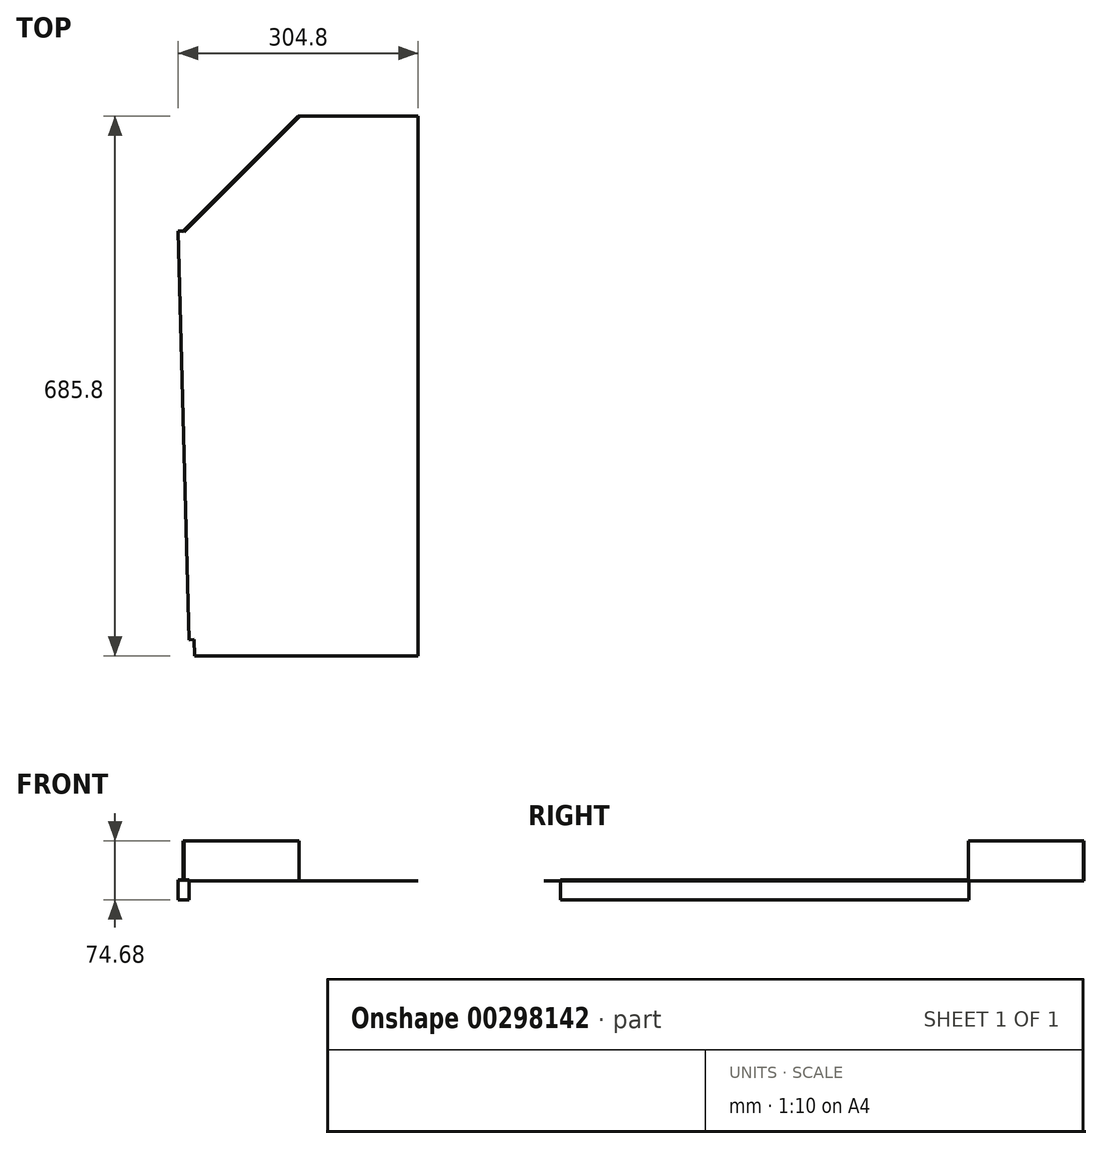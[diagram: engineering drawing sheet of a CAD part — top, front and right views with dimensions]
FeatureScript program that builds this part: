
annotation { "Feature Type Name" : "Feature", "Feature Type Description" : "" }
export const myFeature = defineFeature(function(context is Context, id is Id, definition is map)
    precondition{}
    {
        {
            assignVariable(context, id + "F0", {"name" : "thk", "anyValue" : 0.06});
        }
        {
            var Q0;
            Q0=qCreatedBy(makeId("Top.planeOp"),FACE);
            var sketch = newSketch(context, id + "F1", { "sketchPlane" : qUnion([Q0])});
            skLineSegment(sketch, "E0.bottom", {"start": v(-152.4, 0) * mm, "end": v(0, 0) * mm});
            skLineSegment(sketch, "E0.top", {"start": v(-284.32, -685.8) * mm, "end": v(0, -685.8) * mm});
            skLineSegment(sketch, "E0.right", {"start": v(0, 0) * mm, "end": v(0, -685.8) * mm});
            skLineSegment(sketch, "E1", {"start": v(-298.45, -146.05) * mm, "end": v(-152.4, 0) * mm});
            skLineSegment(sketch, "E2", {"start": v(-304.8, -146.22) * mm, "end": v(-291.21, -665.15) * mm});
            skLineSegment(sketch, "E3", {"start": v(-282.64, -750.07) * mm, "end": v(-303.14, 33.07) * mm, "construction": true});
            skLineSegment(sketch, "E4", {"start": v(-304.8, -146.22) * mm, "end": v(-298.45, -146.05) * mm});
            skLineSegment(sketch, "E5", {"start": v(-291.21, -665.15) * mm, "end": v(-284.86, -664.98) * mm});
            skLineSegment(sketch, "E6", {"start": v(-284.86, -664.98) * mm, "end": v(-284.32, -685.8) * mm});
            skSolve(sketch);
        }
        {
            var Q0;
            Q0 = qSketchRegion(id + "F1", true);
            extrude(context, id + "F2", {"entities" : qUnion([Q0]), "depth" : (getVariable(context, 'thk')) * mm});
        }
        {
            var Q0;
            Q0=makeQuery(id+"F2.opExtrude","SWEPT_FACE",FACE,{"disambiguationData":[OSD([sQuery(id+"F1.wireOp",EDGE,"E2")])]});
            var sketch = newSketch(context, id + "F3", { "sketchPlane" : qUnion([Q0])});
            skLineSegment(sketch, "E7.bottom", {"start": v(657.3, -23.88) * mm, "end": v(138.19, -23.88) * mm});
            skLineSegment(sketch, "E7.top", {"start": v(657.3, 1.52) * mm, "end": v(138.19, 1.52) * mm});
            skLineSegment(sketch, "E7.left", {"start": v(657.3, -23.88) * mm, "end": v(657.3, 1.52) * mm});
            skLineSegment(sketch, "E7.right", {"start": v(138.19, -23.88) * mm, "end": v(138.19, 1.52) * mm});
            skSolve(sketch);
        }
        {
            var Q0;
            Q0 = qSketchRegion(id + "F3", true);
            extrude(context, id + "F4", {"entities" : qUnion([Q0]), "operationType" : NewBodyOperationType.ADD, "oppositeDirection" : true, "depth" : (getVariable(context, 'thk')) * mm});
        }
        {
            var Q0;
            Q0=qCreatedBy(makeId("Top.planeOp"),FACE);
            var sketch = newSketch(context, id + "F5", { "sketchPlane" : qUnion([Q0])});
            skLineSegment(sketch, "E8", {"start": v(-298.45, -146.05) * mm, "end": v(-152.4, 0) * mm});
            skLineSegment(sketch, "E9", {"start": v(-152.4, 0) * mm, "end": v(-151.32, -1.08) * mm});
            skLineSegment(sketch, "E10", {"start": v(-151.32, -1.08) * mm, "end": v(-297.37, -147.13) * mm});
            skLineSegment(sketch, "E11", {"start": v(-297.37, -147.13) * mm, "end": v(-298.45, -146.05) * mm});
            skSolve(sketch);
        }
        {
            var Q0;
            Q0 = qSketchRegion(id + "F5", true);
            extrude(context, id + "F6", {"entities" : qUnion([Q0]), "operationType" : NewBodyOperationType.ADD, "depth" : 50.8 * mm});
        }
        {
            var Q0;
            Q0=qCreatedBy(makeId("Front.planeOp"),FACE);
            var sketch = newSketch(context, id + "F7", { "sketchPlane" : qUnion([Q0])});
            skLineSegment(sketch, "E12", {"start": v(-17.35, 4.65) * mm, "end": v(6.35, 4.65) * mm});
            skLineSegment(sketch, "E13", {"start": v(6.35, 4.65) * mm, "end": v(6.35, -1.7) * mm});
            skLineSegment(sketch, "E14", {"start": v(6.35, -1.7) * mm, "end": v(-17.35, 4.65) * mm});
            skSolve(sketch);
        }
        {
            var Q0;
            Q0 = qSketchRegion(id + "F7", true);
            extrude(context, id + "F8", {"entities" : qUnion([Q0]), "operationType" : NewBodyOperationType.REMOVE, "endBound" : BoundingType.THROUGH_ALL, "depth" : 25.4 * mm});
        }
        {
            var Q0;
            Q0=qCreatedBy(makeId("Right.planeOp"),FACE);
            var sketch = newSketch(context, id + "F9", { "sketchPlane" : qUnion([Q0])});
            skLineSegment(sketch, "E15.MirrorCS", {"start": v(-692.15, 4.65) * mm, "end": v(-692.15, -1.7) * mm});
            skLineSegment(sketch, "E16.MirrorCS", {"start": v(-692.15, -1.7) * mm, "end": v(-668.45, 4.65) * mm});
            skLineSegment(sketch, "E17.MirrorCS", {"start": v(-668.45, 4.65) * mm, "end": v(-692.15, 4.65) * mm});
            skSolve(sketch);
        }
        {
            var Q0;
            Q0 = qSketchRegion(id + "F9", true);
            extrude(context, id + "F10", {"entities" : qUnion([Q0]), "operationType" : NewBodyOperationType.REMOVE, "endBound" : BoundingType.THROUGH_ALL, "oppositeDirection" : true, "depth" : 25.4 * mm});
        }
    });
